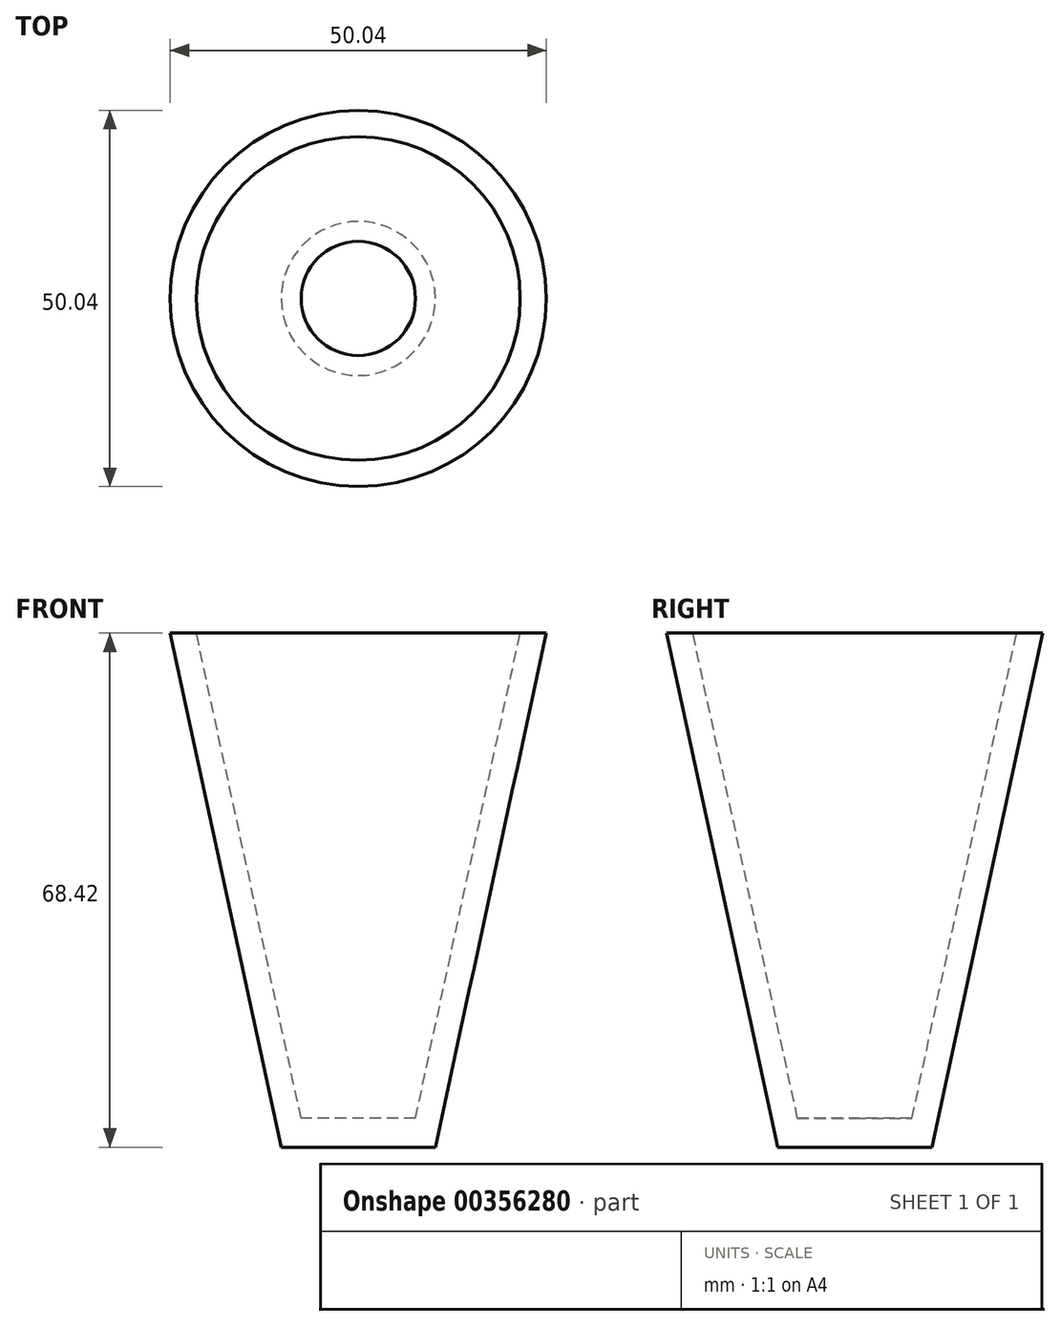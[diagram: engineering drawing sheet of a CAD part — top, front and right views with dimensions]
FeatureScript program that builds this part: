
annotation { "Feature Type Name" : "Feature", "Feature Type Description" : "" }
export const myFeature = defineFeature(function(context is Context, id is Id, definition is map)
    precondition{}
    {
        {
            var Q0;
            Q0=qCreatedBy(makeId("Right.planeOp"),FACE);
            var sketch = newSketch(context, id + "F0", { "sketchPlane" : qUnion([Q0])});
            skLineSegment(sketch, "E0", {"start": v(0, 48.6) * mm, "end": v(0, -24.12) * mm, "construction": true});
            skLineSegment(sketch, "E1", {"start": v(0, 0) * mm, "end": v(10.25, 0) * mm});
            skLineSegment(sketch, "E2", {"start": v(10.25, 0) * mm, "end": v(25.02, 68.42) * mm});
            skLineSegment(sketch, "E3", {"start": v(25.02, 68.42) * mm, "end": v(21.54, 68.42) * mm});
            skLineSegment(sketch, "E4", {"start": v(21.54, 68.42) * mm, "end": v(7.6, 3.84) * mm});
            skLineSegment(sketch, "E5", {"start": v(7.6, 3.84) * mm, "end": v(0, 3.84) * mm});
            skLineSegment(sketch, "E6", {"start": v(0, 3.84) * mm, "end": v(0, 0) * mm});
            skSolve(sketch);
        }
        {
            var Q0;
            Q0=makeQuery(id+"F0.imprint","IMPRINT",FACE,{"disambiguationData":[TD([[makeQuery(id+"F0.imprint","IMPRINT",EDGE,{"derivedFrom":sQuery(id+"F0.wireOp",EDGE,"E1")}),1.0]])]});
            var Q1;
            Q1=sQuery(id+"F0.wireOp",EDGE,"E0");
            revolve(context, id + "F1", {"entities" : qUnion([Q0]), "axis" : qUnion([Q1]), "revolveType" : RevolveType.ONE_DIRECTION, "angle" : 360 * degree});
        }
    });
